# Revit family: LeL Metope 1.2
name_source: partatom
category: Lighting Fixtures
units: mm (PartAtom-declared; Revit-internal decimal feet)

## family parameters
Cut with Voids When Loaded = Yes
Host = Face
Light Source = No
Part Type = Normal
Room Calculation Point = No
Round Connector Dimension = Use Diameter
Shared = No

## types (5) — shared parameters
Alimentazione = 24 V
Apparent Load = 6 VA
CCT = 3000 K
CRI = 80
Default Elevation = 1219 mm
Description = Outdoor Wall Mounted
Height = 60 mm  [stored 0.19685 ft]
IK = IK05
IP = IP65
Lamp = LED
Lenght = 35 mm  [stored 0.114829 ft]
Manufacturer = L&L Luce&Light
Model = TM12
Rated Power supply = 24 V
URL = https://www.lucelight.it
Wattage = 6 W
Weight = 0.17 kg
Widht = 15 mm  [stored 0.0492126 ft]

## per-type parameters (varying)
| type | Lumen Output | Photometry1 | Photometry2 |
| 1.2 DD 6W 24Vdc | 208 lm | TM1 Light source : 1.2 D 3W 24Vdc | TM1 Light source : 1.2 D 3W 24Vdc |
| 1.2 LL 36° 6W 24Vdc | 216 lm | TM1 Light source : 1.2 L 36° 3W 24Vdc | TM1 Light source : 1.2 L 36° 3W 24Vdc |
| 1.2 MM 22° 6W 24Vdc | 232 lm | TM1 Light source : 1.2 M 22° 3W 24Vdc | TM1 Light source : 1.2 M 22° 3W 24Vdc |
| 1.2 SL 17°+36° 6W 24Vdc | 261 lm | TM1 Light source : 1.2 S 17° 3W 24Vdc | TM1 Light source : 1.2 L 36° 3W 24Vdc |
| 1.2 SS 17° 6W 24Vdc | 306 lm | TM1 Light source : 1.2 S 17° 3W 24Vdc | TM1 Light source : 1.2 S 17° 3W 24Vdc |

note: [stored X ft] marks values corroborated as IEEE doubles in the binary element streams (Revit-internal decimal feet)
